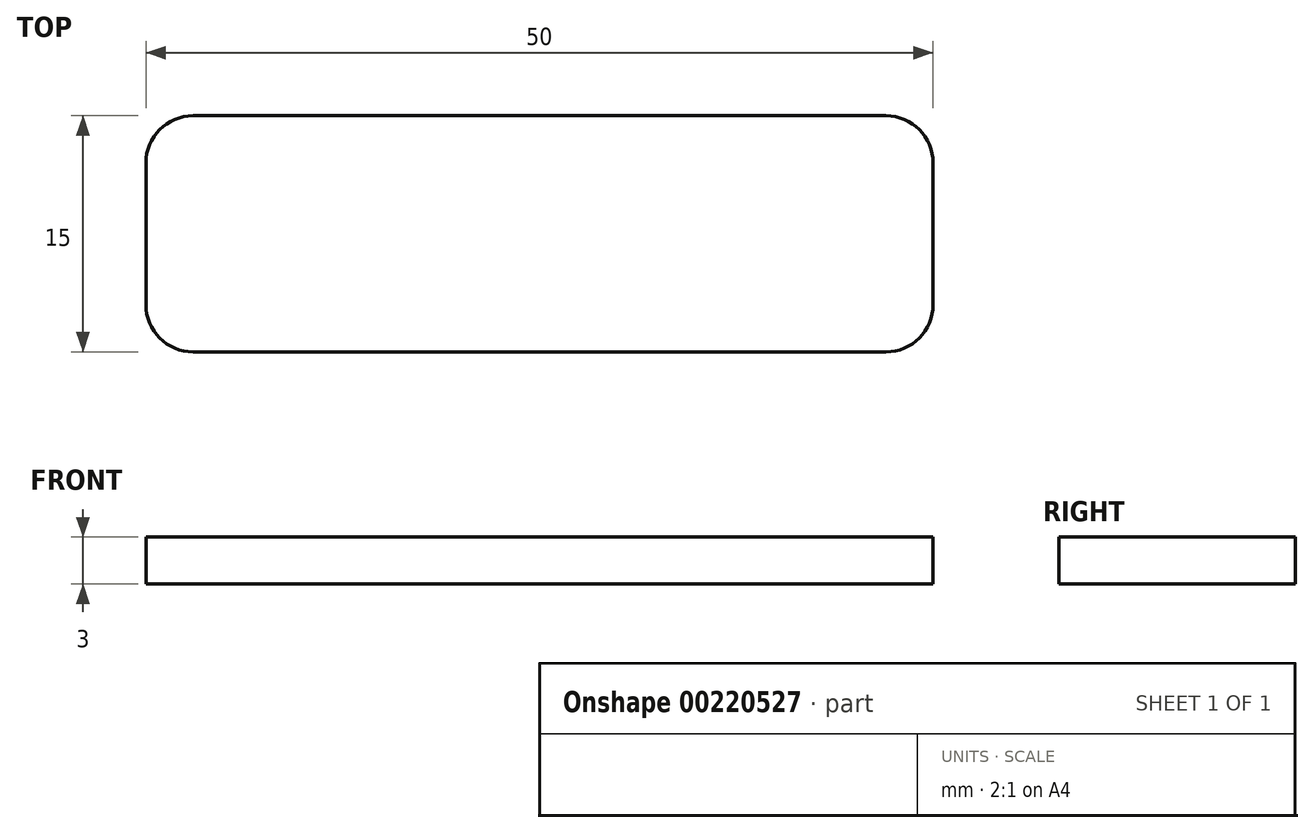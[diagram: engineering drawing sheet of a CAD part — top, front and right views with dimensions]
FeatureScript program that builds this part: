
annotation { "Feature Type Name" : "Feature", "Feature Type Description" : "" }
export const myFeature = defineFeature(function(context is Context, id is Id, definition is map)
    precondition{}
    {
        {
            var Q0;
            Q0=qCreatedBy(makeId("Top.planeOp"),FACE);
            var sketch = newSketch(context, id + "F0", { "sketchPlane" : qUnion([Q0])});
            skLineSegment(sketch, "E0.bottom", {"start": v(25, -7.5) * mm, "end": v(-25, -7.5) * mm});
            skLineSegment(sketch, "E0.top", {"start": v(25, 7.5) * mm, "end": v(-25, 7.5) * mm});
            skLineSegment(sketch, "E0.left", {"start": v(25, -7.5) * mm, "end": v(25, 7.5) * mm});
            skLineSegment(sketch, "E0.right", {"start": v(-25, -7.5) * mm, "end": v(-25, 7.5) * mm});
            skPoint(sketch, "E0.middle", {"position": v(0, 0) * mm});
            skSolve(sketch);
        }
        {
            var Q0;
            Q0 = qSketchRegion(id + "F0", true);
            extrude(context, id + "F1", {"entities" : qUnion([Q0]), "depth" : 3 * mm});
        }
        {
            var Q0;
            Q0=makeQuery(id+"F1.opExtrude","SWEPT_EDGE",EDGE,{"disambiguationData":[OSD([sQuery(id+"F0.wireOp",EDGE,"E0.top"),sQuery(id+"F0.wireOp",EDGE,"E0.right")])]});
            var Q1;
            Q1=makeQuery(id+"F1.opExtrude","SWEPT_EDGE",EDGE,{"disambiguationData":[OSD([sQuery(id+"F0.wireOp",EDGE,"E0.bottom"),sQuery(id+"F0.wireOp",EDGE,"E0.right")])]});
            var Q2;
            Q2=makeQuery(id+"F1.opExtrude","SWEPT_EDGE",EDGE,{"disambiguationData":[OSD([sQuery(id+"F0.wireOp",EDGE,"E0.top"),sQuery(id+"F0.wireOp",EDGE,"E0.left")])]});
            var Q3;
            Q3=makeQuery(id+"F1.opExtrude","SWEPT_EDGE",EDGE,{"disambiguationData":[OSD([sQuery(id+"F0.wireOp",EDGE,"E0.bottom"),sQuery(id+"F0.wireOp",EDGE,"E0.left")])]});
            fillet(context, id + "F2", {"entities" : qUnion([Q0, Q1, Q2, Q3]), "radius" : 3 * mm, "tangentPropagation" : true, "allowEdgeOverflow" : false});
        }
    });
